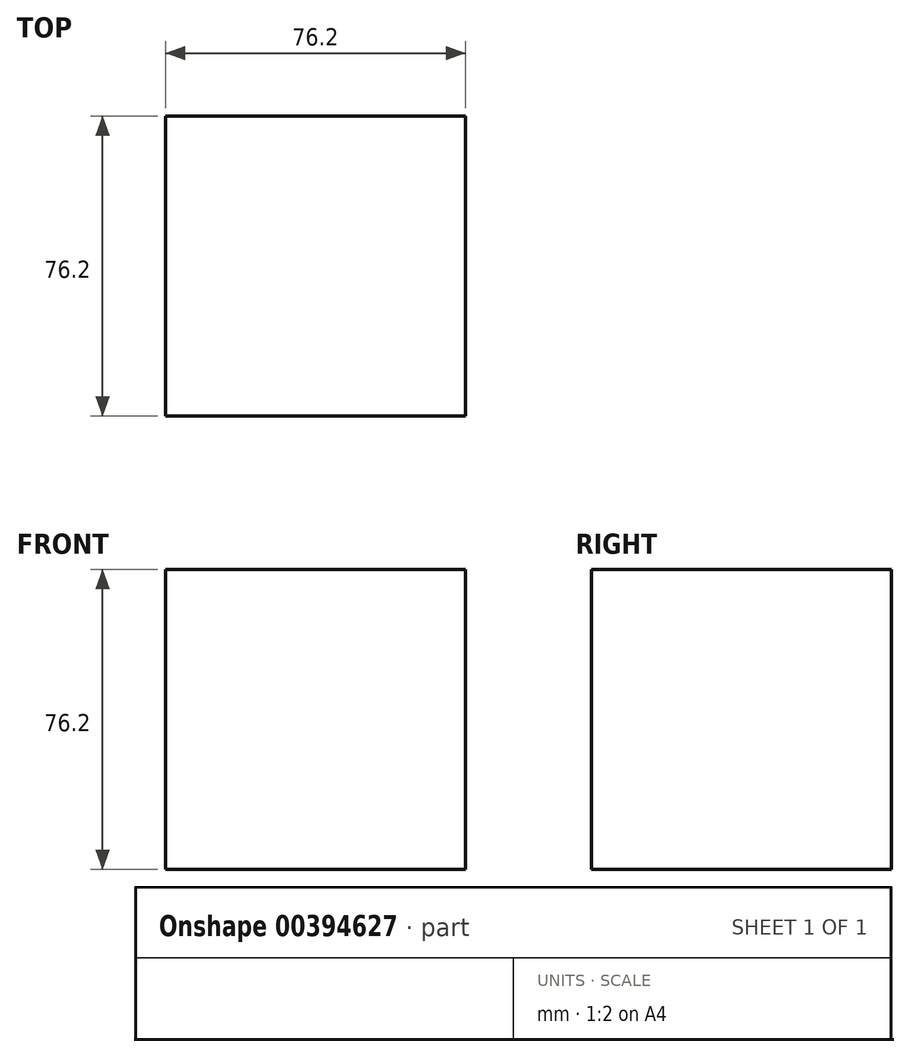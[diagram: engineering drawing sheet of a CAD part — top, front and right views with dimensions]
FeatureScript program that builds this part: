
annotation { "Feature Type Name" : "Feature", "Feature Type Description" : "" }
export const myFeature = defineFeature(function(context is Context, id is Id, definition is map)
    precondition{}
    {
        {
            var Q0;
            Q0=qCreatedBy(makeId("Front.planeOp"),FACE);
            var sketch = newSketch(context, id + "F0", { "sketchPlane" : qUnion([Q0])});
            skLineSegment(sketch, "E0.bottom", {"start": v(-38, -39) * mm, "end": v(38.2, -39) * mm});
            skLineSegment(sketch, "E0.top", {"start": v(-38, 37.2) * mm, "end": v(38.2, 37.2) * mm});
            skLineSegment(sketch, "E0.left", {"start": v(-38, -39) * mm, "end": v(-38, 37.2) * mm});
            skLineSegment(sketch, "E0.right", {"start": v(38.2, -39) * mm, "end": v(38.2, 37.2) * mm});
            skSolve(sketch);
        }
        {
            var Q0;
            Q0=makeQuery(id+"F0.imprint","IMPRINT",FACE,{"disambiguationData":[TD([[makeQuery(id+"F0.imprint","IMPRINT",EDGE,{"derivedFrom":sQuery(id+"F0.wireOp",EDGE,"E0.bottom")}),1.0]])]});
            extrude(context, id + "F1", {"entities" : qUnion([Q0]), "depth" : 76.2 * mm});
        }
    });
